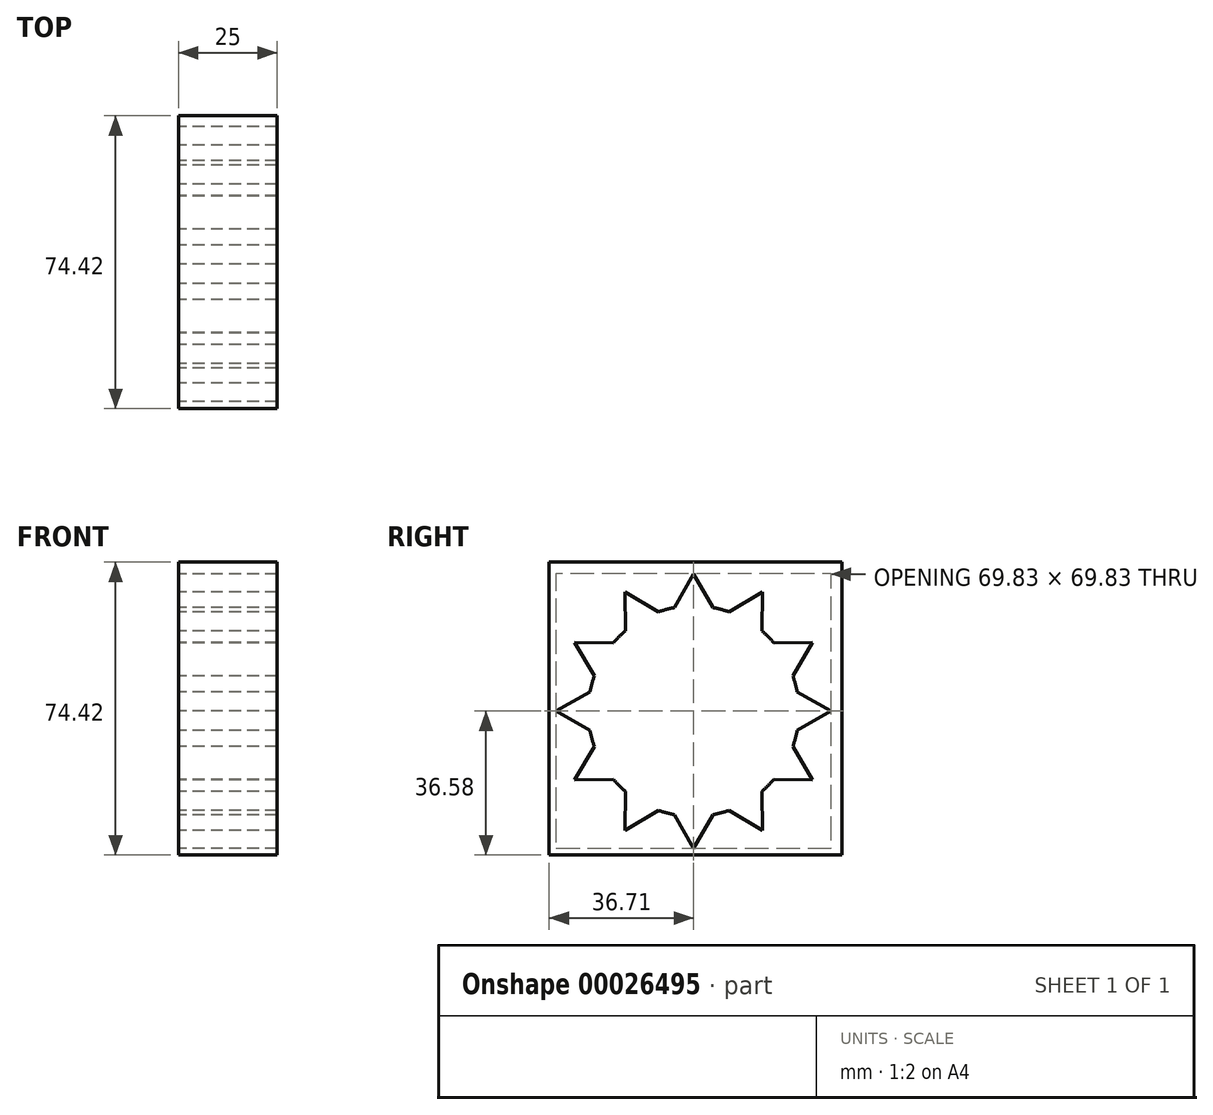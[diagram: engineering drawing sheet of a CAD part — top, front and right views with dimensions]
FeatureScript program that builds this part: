
annotation { "Feature Type Name" : "Feature", "Feature Type Description" : "" }
export const myFeature = defineFeature(function(context is Context, id is Id, definition is map)
    precondition{}
    {
        {
            var Q0;
            Q0=qCreatedBy(makeId("Right.planeOp"),FACE);
            var sketch = newSketch(context, id + "F0", { "sketchPlane" : qUnion([Q0])});
            skCircle(sketch, "E0", {"center": v(0, 0) * mm, "radius": 26.76 * mm});
            skLineSegment(sketch, "E1", {"start": v(26.31, 4.87) * mm, "end": v(34.91, 0) * mm});
            skLineSegment(sketch, "E2", {"start": v(34.91, 0) * mm, "end": v(26.31, -4.87) * mm});
            skLineSegment(sketch, "E3.1.0", {"start": v(20.35, 17.37) * mm, "end": v(30.24, 17.46) * mm});
            skLineSegment(sketch, "E3.1.1", {"start": v(30.24, 17.46) * mm, "end": v(25.22, 8.94) * mm});
            skLineSegment(sketch, "E3.2.0", {"start": v(8.94, 25.22) * mm, "end": v(17.46, 30.24) * mm});
            skLineSegment(sketch, "E3.2.1", {"start": v(17.46, 30.24) * mm, "end": v(17.37, 20.35) * mm});
            skLineSegment(sketch, "E3.3.0", {"start": v(-4.87, 26.31) * mm, "end": v(0, 34.91) * mm});
            skLineSegment(sketch, "E3.3.1", {"start": v(0, 34.91) * mm, "end": v(4.87, 26.31) * mm});
            skLineSegment(sketch, "E3.4.0", {"start": v(-17.37, 20.35) * mm, "end": v(-17.46, 30.24) * mm});
            skLineSegment(sketch, "E3.4.1", {"start": v(-17.46, 30.24) * mm, "end": v(-8.94, 25.22) * mm});
            skLineSegment(sketch, "E3.5.0", {"start": v(-25.22, 8.94) * mm, "end": v(-30.24, 17.46) * mm});
            skLineSegment(sketch, "E3.5.1", {"start": v(-30.24, 17.46) * mm, "end": v(-20.35, 17.37) * mm});
            skLineSegment(sketch, "E3.6.0", {"start": v(-26.31, -4.87) * mm, "end": v(-34.91, 0) * mm});
            skLineSegment(sketch, "E3.6.1", {"start": v(-34.91, 0) * mm, "end": v(-26.31, 4.87) * mm});
            skLineSegment(sketch, "E3.7.0", {"start": v(-20.35, -17.37) * mm, "end": v(-30.24, -17.46) * mm});
            skLineSegment(sketch, "E3.7.1", {"start": v(-30.24, -17.46) * mm, "end": v(-25.22, -8.94) * mm});
            skLineSegment(sketch, "E3.8.0", {"start": v(-8.94, -25.22) * mm, "end": v(-17.46, -30.24) * mm});
            skLineSegment(sketch, "E3.8.1", {"start": v(-17.46, -30.24) * mm, "end": v(-17.37, -20.35) * mm});
            skLineSegment(sketch, "E3.9.0", {"start": v(4.87, -26.31) * mm, "end": v(0, -34.91) * mm});
            skLineSegment(sketch, "E3.9.1", {"start": v(0, -34.91) * mm, "end": v(-4.87, -26.31) * mm});
            skLineSegment(sketch, "E3.10.0", {"start": v(17.37, -20.35) * mm, "end": v(17.46, -30.24) * mm});
            skLineSegment(sketch, "E3.10.1", {"start": v(17.46, -30.24) * mm, "end": v(8.94, -25.22) * mm});
            skLineSegment(sketch, "E3.11.0", {"start": v(25.22, -8.94) * mm, "end": v(30.24, -17.46) * mm});
            skLineSegment(sketch, "E3.11.1", {"start": v(30.24, -17.46) * mm, "end": v(20.35, -17.37) * mm});
            skSolve(sketch);
        }
        {
            var Q0;
            {var subQ1=sQuery(id+"F0.wireOp",EDGE,"E3.1.0");Q0=makeQuery(id+"F0.imprint","IMPRINT",FACE,{"disambiguationData":[TD([[makeQuery(id+"F0.imprint","IMPRINT",EDGE,{"derivedFrom":subQ1}),-1.0]])]});}
            var Q1;
            {var subQ1=sQuery(id+"F0.wireOp",EDGE,"E3.2.0");Q1=makeQuery(id+"F0.imprint","IMPRINT",FACE,{"disambiguationData":[TD([[makeQuery(id+"F0.imprint","IMPRINT",EDGE,{"derivedFrom":subQ1}),-1.0]])]});}
            var Q2;
            {var subQ1=sQuery(id+"F0.wireOp",EDGE,"E3.3.0");Q2=makeQuery(id+"F0.imprint","IMPRINT",FACE,{"disambiguationData":[TD([[makeQuery(id+"F0.imprint","IMPRINT",EDGE,{"derivedFrom":subQ1}),-1.0]])]});}
            var Q3;
            {var subQ1=sQuery(id+"F0.wireOp",EDGE,"E3.4.0");Q3=makeQuery(id+"F0.imprint","IMPRINT",FACE,{"disambiguationData":[TD([[makeQuery(id+"F0.imprint","IMPRINT",EDGE,{"derivedFrom":subQ1}),-1.0]])]});}
            var Q4;
            {var subQ1=sQuery(id+"F0.wireOp",EDGE,"E3.5.0");Q4=makeQuery(id+"F0.imprint","IMPRINT",FACE,{"disambiguationData":[TD([[makeQuery(id+"F0.imprint","IMPRINT",EDGE,{"derivedFrom":subQ1}),-1.0]])]});}
            var Q5;
            {var subQ1=sQuery(id+"F0.wireOp",EDGE,"E3.6.0");Q5=makeQuery(id+"F0.imprint","IMPRINT",FACE,{"disambiguationData":[TD([[makeQuery(id+"F0.imprint","IMPRINT",EDGE,{"derivedFrom":subQ1}),-1.0]])]});}
            var Q6;
            {var subQ1=sQuery(id+"F0.wireOp",EDGE,"E3.7.0");Q6=makeQuery(id+"F0.imprint","IMPRINT",FACE,{"disambiguationData":[TD([[makeQuery(id+"F0.imprint","IMPRINT",EDGE,{"derivedFrom":subQ1}),-1.0]])]});}
            var Q7;
            {var subQ1=sQuery(id+"F0.wireOp",EDGE,"E3.8.0");Q7=makeQuery(id+"F0.imprint","IMPRINT",FACE,{"disambiguationData":[TD([[makeQuery(id+"F0.imprint","IMPRINT",EDGE,{"derivedFrom":subQ1}),-1.0]])]});}
            var Q8;
            {var subQ1=sQuery(id+"F0.wireOp",EDGE,"E3.9.0");Q8=makeQuery(id+"F0.imprint","IMPRINT",FACE,{"disambiguationData":[TD([[makeQuery(id+"F0.imprint","IMPRINT",EDGE,{"derivedFrom":subQ1}),-1.0]])]});}
            var Q9;
            {var subQ1=sQuery(id+"F0.wireOp",EDGE,"E3.10.0");Q9=makeQuery(id+"F0.imprint","IMPRINT",FACE,{"disambiguationData":[TD([[makeQuery(id+"F0.imprint","IMPRINT",EDGE,{"derivedFrom":subQ1}),-1.0]])]});}
            var Q10;
            {var subQ1=sQuery(id+"F0.wireOp",EDGE,"E3.11.0");Q10=makeQuery(id+"F0.imprint","IMPRINT",FACE,{"disambiguationData":[TD([[makeQuery(id+"F0.imprint","IMPRINT",EDGE,{"derivedFrom":subQ1}),-1.0]])]});}
            var Q11;
            {var subQ0=sQuery(id+"F0.wireOp",EDGE,"E1");Q11=makeQuery(id+"F0.imprint","IMPRINT",FACE,{"disambiguationData":[TD([[makeQuery(id+"F0.imprint","IMPRINT",EDGE,{"derivedFrom":subQ0}),-1.0]])]});}
            var Q12;
            {var subQ0=sQuery(id+"F0.wireOp",EDGE,"E0");var subQ2=makeQuery(id+"F0.imprint","INTERSECT",VERTEX,{"derivedFrom":[subQ0,sQuery(id+"F0.wireOp",EDGE,"E1")]});Q12=makeQuery(id+"F0.imprint","IMPRINT",FACE,{"disambiguationData":[TD([[makeQuery(id+"F0.imprint","IMPRINT",EDGE,{"disambiguationData":[TD([[subQ2,-1.0]])],"derivedFrom":subQ0}),1.0]])]});}
            extrude(context, id + "F1", {"entities" : qUnion([Q0, Q1, Q2, Q3, Q4, Q5, Q6, Q7, Q8, Q9, Q10, Q11, Q12]), "depth" : 25 * mm});
        }
        {
            var Q0;
            Q0=qCreatedBy(makeId("Right.planeOp"),FACE);
            var sketch = newSketch(context, id + "F2", { "sketchPlane" : qUnion([Q0])});
            skLineSegment(sketch, "E4.bottom", {"start": v(-36.7, 37.84) * mm, "end": v(37.71, 37.84) * mm});
            skLineSegment(sketch, "E4.top", {"start": v(-36.7, -36.58) * mm, "end": v(37.71, -36.58) * mm});
            skLineSegment(sketch, "E4.left", {"start": v(-36.7, 37.84) * mm, "end": v(-36.7, -36.58) * mm});
            skLineSegment(sketch, "E4.right", {"start": v(37.71, 37.84) * mm, "end": v(37.71, -36.58) * mm});
            skSolve(sketch);
        }
        {
            var Q0;
            Q0=makeQuery(id+"F2.imprint","IMPRINT",FACE,{"disambiguationData":[TD([[makeQuery(id+"F2.imprint","IMPRINT",EDGE,{"derivedFrom":sQuery(id+"F2.wireOp",EDGE,"E4.bottom")}),-1.0]])]});
            extrude(context, id + "F3", {"entities" : qUnion([Q0]), "depth" : 25 * mm});
        }
        {
            var Q0;
            Q0=makeQuery(id+"F1.opExtrude","SWEPT_BODY",BODY,{"disambiguationData":[OSD([sQuery(id+"F0.wireOp",EDGE,"E0"),sQuery(id+"F0.wireOp",EDGE,"E1"),sQuery(id+"F0.wireOp",EDGE,"E2"),sQuery(id+"F0.wireOp",EDGE,"E3.1.0"),sQuery(id+"F0.wireOp",EDGE,"E3.1.1"),sQuery(id+"F0.wireOp",EDGE,"E3.2.0"),sQuery(id+"F0.wireOp",EDGE,"E3.2.1"),sQuery(id+"F0.wireOp",EDGE,"E3.3.0"),sQuery(id+"F0.wireOp",EDGE,"E3.3.1"),sQuery(id+"F0.wireOp",EDGE,"E3.4.0"),sQuery(id+"F0.wireOp",EDGE,"E3.4.1"),sQuery(id+"F0.wireOp",EDGE,"E3.5.0"),sQuery(id+"F0.wireOp",EDGE,"E3.5.1"),sQuery(id+"F0.wireOp",EDGE,"E3.6.0"),sQuery(id+"F0.wireOp",EDGE,"E3.6.1"),sQuery(id+"F0.wireOp",EDGE,"E3.7.0"),sQuery(id+"F0.wireOp",EDGE,"E3.7.1"),sQuery(id+"F0.wireOp",EDGE,"E3.8.0"),sQuery(id+"F0.wireOp",EDGE,"E3.8.1"),sQuery(id+"F0.wireOp",EDGE,"E3.9.0"),sQuery(id+"F0.wireOp",EDGE,"E3.9.1"),sQuery(id+"F0.wireOp",EDGE,"E3.10.0"),sQuery(id+"F0.wireOp",EDGE,"E3.10.1"),sQuery(id+"F0.wireOp",EDGE,"E3.11.0"),sQuery(id+"F0.wireOp",EDGE,"E3.11.1")])]});
            var Q1;
            Q1=makeQuery(id+"F3.opExtrude","SWEPT_BODY",BODY,{"disambiguationData":[OSD([sQuery(id+"F2.wireOp",EDGE,"E4.bottom"),sQuery(id+"F2.wireOp",EDGE,"E4.top"),sQuery(id+"F2.wireOp",EDGE,"E4.left"),sQuery(id+"F2.wireOp",EDGE,"E4.right")])]});
            booleanBodies(context, id + "F4", {"operationType" : BooleanOperationType.SUBTRACTION, "tools" : qUnion([Q0]), "targets" : qUnion([Q1])});
        }
    });
